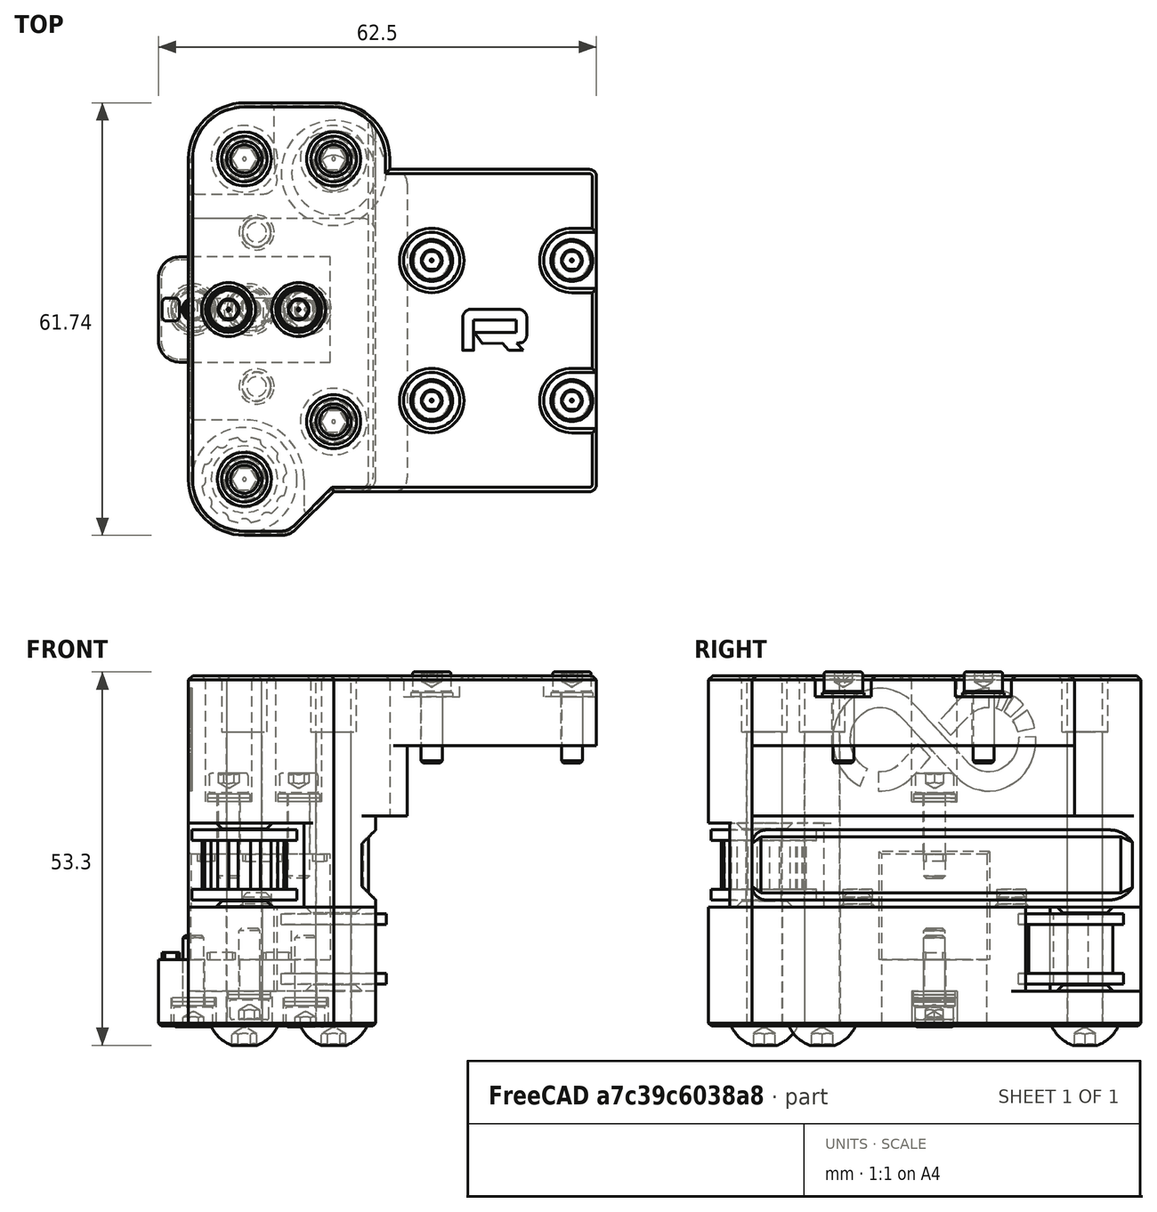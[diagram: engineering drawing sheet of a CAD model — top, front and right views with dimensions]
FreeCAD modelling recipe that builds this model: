
FCSTD DOCUMENT  (FreeCAD 0.19R24291 (Git))
Label: y-carrier-right-1515-assembly
License: Other
LicenseURL: GPL3
objects: Part::FeaturePython×27, Part::Feature×4, App::Part×1
note: 31 computed .brp shape members not serialized (recipe doc carries the construction recipe); baked Part::Feature solids carry a one-line shape summary decoded from their .brp

FEATURE [Part::Feature] Part__Mirroring002001  label="20t-idler"
  Placement = pos=(0,-4.61,0) rot=(0,0,1;0rad)
  shape: bbox 15 x 15 x 10 mm, 31 faces (baked)
FEATURE [Part::Feature] Part__Mirroring003001  label="smooth-idler"
  Placement = pos=(2,0.5,0) rot=(0,0,1;0rad)
  shape: bbox 15 x 15 x 10 mm, 8 faces (baked)
FEATURE [Part::FeaturePython] Screw002  label="M5x50-Screw"  # Fasteners workbench fastener (typed FeaturePython)
  Placement = pos=(-9,21.5,3) rot=(-1,0,0;3.14159rad)
  diameter = 3
  invert = false
  length = 11
  lengthCustom = 50
  matchOuter = true
  offset = 0
  thread = false
  type = 39
FEATURE [Part::FeaturePython] Screw003  label="M5x50-Screw004"  # Fasteners workbench fastener (typed FeaturePython)
  Placement = pos=(-21.74,21.5,3) rot=(-1,0,0;3.14159rad)
  diameter = 3
  invert = false
  length = 11
  lengthCustom = 50
  matchOuter = true
  offset = 0
  thread = false
  type = 39
FEATURE [Part::FeaturePython] Screw004  label="M5x50-Screw005"  # Fasteners workbench fastener (typed FeaturePython)
  Placement = pos=(-9,-16,3) rot=(-1,0,0;3.14159rad)
  diameter = 3
  invert = false
  length = 11
  lengthCustom = 50
  matchOuter = true
  offset = 0
  thread = false
  type = 39
FEATURE [Part::FeaturePython] Screw005  label="M5x50-Screw006"  # Fasteners workbench fastener (typed FeaturePython)
  Placement = pos=(-21.74,-24.24,3) rot=(-1,0,0;3.14159rad)
  diameter = 3
  invert = false
  length = 11
  lengthCustom = 50
  matchOuter = true
  offset = 0
  thread = false
  type = 39
FEATURE [Part::FeaturePython] Washer002  label="M3-Washer"  # Fasteners workbench fastener (typed FeaturePython)
  Placement = pos=(25,7,50) rot=(0,0,1;0rad)
  diameter = 4
  invert = true
  matchOuter = true
  offset = 0
  type = 5
FEATURE [Part::FeaturePython] Washer003  label="M3-Washer007"  # Fasteners workbench fastener (typed FeaturePython)
  Placement = pos=(25,-13,50) rot=(0,0,1;0rad)
  diameter = 4
  invert = true
  matchOuter = true
  offset = 0
  type = 5
FEATURE [Part::FeaturePython] Washer004  label="M3-Washer009"  # Fasteners workbench fastener (typed FeaturePython)
  Placement = pos=(5,-13,50) rot=(0,0,1;0rad)
  diameter = 4
  invert = true
  matchOuter = true
  offset = 0
  type = 5
FEATURE [Part::FeaturePython] Washer005  label="M3-Washer008"  # Fasteners workbench fastener (typed FeaturePython)
  Placement = pos=(5,7,50) rot=(0,0,1;0rad)
  diameter = 4
  invert = true
  matchOuter = true
  offset = 0
  type = 5
FEATURE [Part::FeaturePython] Screw006  label="M3x10-Screw"  # Fasteners workbench fastener (typed FeaturePython)
  Placement = pos=(25,-13,50.55) rot=(0,0,1;0rad)
  baseObject = -> Washer003 [Edge1]
  diameter = 4
  invert = false
  length = 3
  lengthCustom = 10
  matchOuter = true
  offset = 0
  thread = false
  type = 33
FEATURE [Part::FeaturePython] Screw007  label="M3x10-Screw005"  # Fasteners workbench fastener (typed FeaturePython)
  Placement = pos=(5,-13,50.55) rot=(0,0,1;0rad)
  baseObject = -> Washer004 [Edge1]
  diameter = 4
  invert = false
  length = 3
  lengthCustom = 10
  matchOuter = true
  offset = 0
  thread = false
  type = 33
FEATURE [Part::FeaturePython] Screw008  label="M3x10-Screw004"  # Fasteners workbench fastener (typed FeaturePython)
  Placement = pos=(5,7,50.55) rot=(0,0,1;0rad)
  baseObject = -> Washer005 [Edge1]
  diameter = 4
  invert = false
  length = 3
  lengthCustom = 10
  matchOuter = true
  offset = 0
  thread = false
  type = 33
FEATURE [Part::FeaturePython] Screw009  label="M3x10-Screw003"  # Fasteners workbench fastener (typed FeaturePython)
  Placement = pos=(25,7,50.55) rot=(0,0,1;0rad)
  baseObject = -> Washer002 [Edge1]
  diameter = 4
  invert = false
  length = 3
  lengthCustom = 10
  matchOuter = true
  offset = 0
  thread = false
  type = 33
FEATURE [Part::Feature] Chamfer010001
  Placement = pos=(0,0,3) rot=(0,0,1;0rad)
  shape: bbox 31 x 61.74 x 19 mm, 118 faces (baked)
FEATURE [Part::Feature] Cut001001
  Placement = pos=(0,0,3) rot=(0,0,1;0rad)
  shape: bbox 58.24 x 61.74 x 33.85 mm, 483 faces (baked)
FEATURE [Part::FeaturePython] Washer  label="M3-Washer010"  # Fasteners workbench fastener (typed FeaturePython)
  Placement = pos=(-13,0,7) rot=(-1,0,0;3.14159rad)
  baseObject = -> Chamfer010001 [Edge6]
  diameter = 4
  invert = false
  matchOuter = true
  offset = 0
  type = 5
FEATURE [Part::FeaturePython] Washer006  label="M3-Washer011"  # Fasteners workbench fastener (typed FeaturePython)
  Placement = pos=(-29,0,7) rot=(-1,0,0;3.14159rad)
  baseObject = -> Chamfer010001 [Edge211]
  diameter = 4
  invert = false
  matchOuter = true
  offset = 0
  type = 5
FEATURE [Part::FeaturePython] Washer007  label="M3-Washer018"  # Fasteners workbench fastener (typed FeaturePython)
  Placement = pos=(-21,0,8) rot=(-1,0,0;3.14159rad)
  baseObject = -> Chamfer010001 [Edge213]
  diameter = 4
  invert = false
  matchOuter = true
  offset = 0
  type = 5
FEATURE [Part::FeaturePython] Washer008  label="M3-Washer019"  # Fasteners workbench fastener (typed FeaturePython)
  Placement = pos=(-13,1e-16,6.45) rot=(-1,0,0;3.14159rad)
  baseObject = -> Washer [Edge1]
  diameter = 4
  invert = false
  matchOuter = true
  offset = 0
  type = 5
FEATURE [Part::FeaturePython] Washer009  label="M3-Washer020"  # Fasteners workbench fastener (typed FeaturePython)
  Placement = pos=(-21,1e-16,7.45) rot=(-1,0,0;3.14159rad)
  baseObject = -> Washer007 [Edge1]
  diameter = 4
  invert = false
  matchOuter = true
  offset = 0
  type = 5
FEATURE [Part::FeaturePython] Washer010  label="M3-Washer013"  # Fasteners workbench fastener (typed FeaturePython)
  Placement = pos=(-29,1e-16,6.45) rot=(-1,0,0;3.14159rad)
  baseObject = -> Washer006 [Edge1]
  diameter = 4
  invert = false
  matchOuter = true
  offset = 0
  type = 5
FEATURE [Part::FeaturePython] Screw  label="M3x10-Screw009"  # Fasteners workbench fastener (typed FeaturePython)
  Placement = pos=(-13,1e-16,5.9) rot=(-1,0,0;3.14159rad)
  baseObject = -> Washer008 [Edge1]
  diameter = 4
  invert = false
  length = 3
  lengthCustom = 10
  matchOuter = true
  offset = 0
  thread = false
  type = 33
FEATURE [Part::FeaturePython] Screw010  label="M3x10-Screw007"  # Fasteners workbench fastener (typed FeaturePython)
  Placement = pos=(-29,1e-16,5.9) rot=(-1,0,0;3.14159rad)
  baseObject = -> Washer010 [Edge1]
  diameter = 4
  invert = false
  length = 3
  lengthCustom = 10
  matchOuter = true
  offset = 0
  thread = false
  type = 33
FEATURE [Part::FeaturePython] Screw011  label="M3x10-Screw010"  # Fasteners workbench fastener (typed FeaturePython)
  Placement = pos=(-21,1e-16,6.9) rot=(-1,0,0;3.14159rad)
  baseObject = -> Washer009 [Edge1]
  diameter = 4
  invert = false
  length = 3
  lengthCustom = 10
  matchOuter = true
  offset = 0
  thread = false
  type = 33
FEATURE [Part::FeaturePython] Washer011  label="M3-Washer014"  # Fasteners workbench fastener (typed FeaturePython)
  Placement = pos=(-14,0,35) rot=(0,0,1;0rad)
  baseObject = -> Cut001001 [Edge1162]
  diameter = 4
  invert = false
  matchOuter = true
  offset = 0
  type = 5
FEATURE [Part::FeaturePython] Washer012  label="M3-Washer015"  # Fasteners workbench fastener (typed FeaturePython)
  Placement = pos=(-24,0,35) rot=(0,0,1;0rad)
  baseObject = -> Cut001001 [Edge1160]
  diameter = 4
  invert = false
  matchOuter = true
  offset = 0
  type = 5
FEATURE [Part::FeaturePython] Washer013  label="M3-Washer016"  # Fasteners workbench fastener (typed FeaturePython)
  Placement = pos=(-14,0,35.55) rot=(0,0,1;0rad)
  baseObject = -> Washer011 [Edge1]
  diameter = 4
  invert = false
  matchOuter = true
  offset = 0
  type = 5
FEATURE [Part::FeaturePython] Washer014  label="M3-Washer017"  # Fasteners workbench fastener (typed FeaturePython)
  Placement = pos=(-24,0,35.55) rot=(0,0,1;0rad)
  baseObject = -> Washer012 [Edge1]
  diameter = 4
  invert = false
  matchOuter = true
  offset = 0
  type = 5
FEATURE [Part::FeaturePython] Screw012  label="M3x12-Screw"  # Fasteners workbench fastener (typed FeaturePython)
  Placement = pos=(-14,0,36.1) rot=(0,0,1;0rad)
  baseObject = -> Washer013 [Edge1]
  diameter = 4
  invert = false
  length = 4
  lengthCustom = 12
  matchOuter = true
  offset = 0
  thread = false
  type = 33
FEATURE [Part::FeaturePython] Screw013  label="M3x12-Screw001"  # Fasteners workbench fastener (typed FeaturePython)
  Placement = pos=(-24,0,36.1) rot=(0,0,1;0rad)
  baseObject = -> Washer014 [Edge1]
  diameter = 4
  invert = false
  length = 4
  lengthCustom = 12
  matchOuter = true
  offset = 0
  thread = false
  type = 33
FEATURE [App::Part] Part  label="Y-carrier-right"
  Group = -> [Part__Mirroring002001,Part__Mirroring003001,Screw003,Screw004,Screw005,Screw002,Screw006,Screw009,Screw008,Screw007,Washer005,Washer004,Washer003,Washer002,Chamfer010001,Cut001001,Washer010,Screw010,Washer008,Screw011,Washer006,Washer009,Screw,Washer007,Washer,Washer013,Washer014,Washer012,Screw013,Screw012,Washer011]
  Origin = -> Origin
